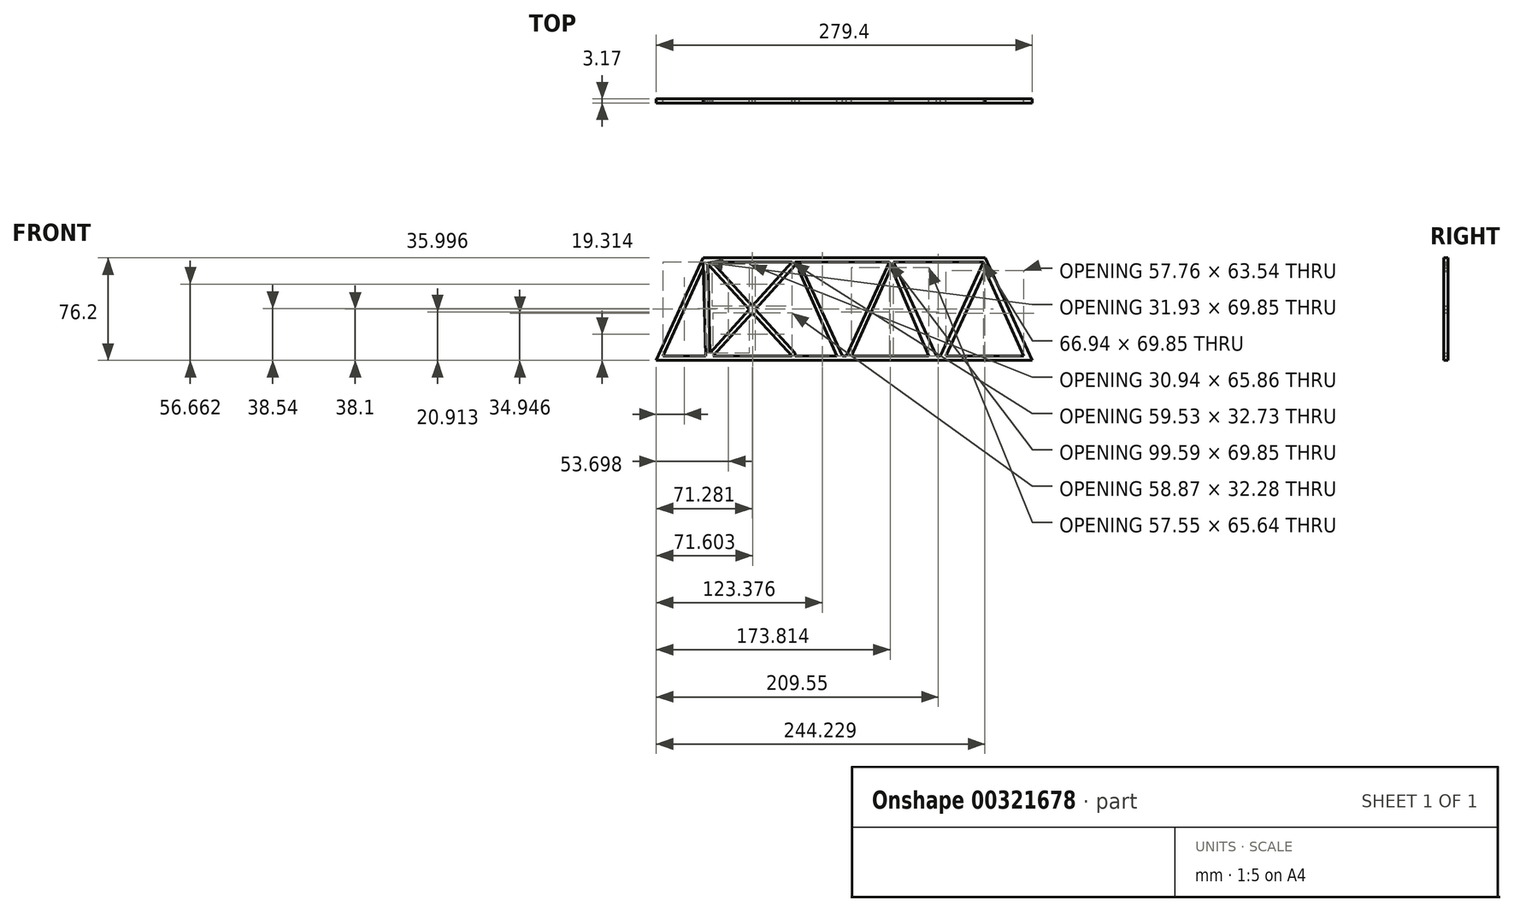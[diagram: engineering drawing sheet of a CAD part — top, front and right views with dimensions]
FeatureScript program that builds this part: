
annotation { "Feature Type Name" : "Feature", "Feature Type Description" : "" }
export const myFeature = defineFeature(function(context is Context, id is Id, definition is map)
    precondition{}
    {
        {
            var Q0;
            Q0=qCreatedBy(makeId("Front.planeOp"),FACE);
            var sketch = newSketch(context, id + "F0", { "sketchPlane" : qUnion([Q0])});
            skLineSegment(sketch, "E0", {"start": v(-139.7, 0) * mm, "end": v(139.7, 0) * mm});
            skLineSegment(sketch, "E1", {"start": v(-139.7, 0) * mm, "end": v(-104.78, 76.2) * mm});
            skLineSegment(sketch, "E2", {"start": v(-101.6, 76.2) * mm, "end": v(104.78, 76.2) * mm});
            skLineSegment(sketch, "E3", {"start": v(104.77, 76.2) * mm, "end": v(139.7, 0) * mm});
            skLineSegment(sketch, "E4", {"start": v(-1.46, 3.18) * mm, "end": v(-33.47, 73.03) * mm});
            skLineSegment(sketch, "E5", {"start": v(1.46, 3.18) * mm, "end": v(33.47, 73.03) * mm});
            skLineSegment(sketch, "E6", {"start": v(36.38, 73.03) * mm, "end": v(68.4, 3.17) * mm});
            skLineSegment(sketch, "E7", {"start": v(71.3, 3.17) * mm, "end": v(103.32, 73.03) * mm});
            skLineSegment(sketch, "E8", {"start": v(34.92, 73.03) * mm, "end": v(34.92, 3.17) * mm});
            skLineSegment(sketch, "E9", {"start": v(69.85, 3.17) * mm, "end": v(69.85, 76.2) * mm});
            skLineSegment(sketch, "E10", {"start": v(104.78, 76.2) * mm, "end": v(104.78, 0) * mm});
            skLineSegment(sketch, "E11", {"start": v(-104.76, 68.62) * mm, "end": v(-134.75, 3.18) * mm});
            skLineSegment(sketch, "E12", {"start": v(-134.75, 3.18) * mm, "end": v(-102.82, 3.18) * mm});
            skLineSegment(sketch, "E13.MirrorCS", {"start": v(-71.44, 3.18) * mm, "end": v(-99.65, 3.17) * mm});
            skLineSegment(sketch, "E14", {"start": v(-101.51, 73.03) * mm, "end": v(104.78, 73.03) * mm});
            skPoint(sketch, "E15.orphan", {"position": v(-34.93, 76.2) * mm});
            skPoint(sketch, "E16.orphan", {"position": v(34.92, 76.2) * mm});
            skLineSegment(sketch, "E17", {"start": v(-104.78, 76.2) * mm, "end": v(-104.76, 73.03) * mm});
            skLineSegment(sketch, "E18", {"start": v(-104.76, 73.03) * mm, "end": v(-104.76, 68.62) * mm});
            skLineSegment(sketch, "E19", {"start": v(-104.76, 73.03) * mm, "end": v(-104.7, 73.02) * mm});
            skLineSegment(sketch, "E20", {"start": v(-104.78, 76.2) * mm, "end": v(-102.82, 3.17) * mm});
            skLineSegment(sketch, "E21", {"start": v(-101.6, 76.2) * mm, "end": v(-99.65, 3.17) * mm});
            skLineSegment(sketch, "E22", {"start": v(-104.78, 76.2) * mm, "end": v(-101.6, 76.2) * mm});
            skLineSegment(sketch, "E23", {"start": v(-102.82, 3.17) * mm, "end": v(-99.65, 3.17) * mm});
            skLineSegment(sketch, "E24", {"start": v(-71.44, 3.18) * mm, "end": v(138.24, 3.18) * mm});
            skPoint(sketch, "E25.start.orphan", {"position": v(-69.85, 0) * mm});
            skPoint(sketch, "E26.orphan", {"position": v(0, 0) * mm});
            skPoint(sketch, "E27.orphan", {"position": v(69.85, 0) * mm});
            skLineSegment(sketch, "E28.bottom", {"start": v(-36.51, 3.18) * mm, "end": v(-33.34, 3.18) * mm});
            skLineSegment(sketch, "E28.top", {"start": v(-36.51, 73.03) * mm, "end": v(-33.34, 73.03) * mm});
            skLineSegment(sketch, "E28.left", {"start": v(-36.51, 3.17) * mm, "end": v(-36.51, 73.02) * mm});
            skLineSegment(sketch, "E28.right", {"start": v(-33.34, 3.17) * mm, "end": v(-33.34, 73.02) * mm});
            skLineSegment(sketch, "E29.0", {"start": v(-98.19, 73.03) * mm, "end": v(-68.3, 40.3) * mm});
            skLineSegment(sketch, "E30.0", {"start": v(-101.47, 71.47) * mm, "end": v(-70.53, 37.83) * mm});
            skLineSegment(sketch, "E31.trimOffspring", {"start": v(-66.12, 37.92) * mm, "end": v(-36.51, 5.5) * mm});
            skLineSegment(sketch, "E32.trimOffspring", {"start": v(-68.35, 35.45) * mm, "end": v(-38.66, 3.17) * mm});
            skLineSegment(sketch, "E33.0", {"start": v(-38.65, 73.03) * mm, "end": v(-68.3, 40.3) * mm});
            skLineSegment(sketch, "E34.0", {"start": v(-36.51, 70.66) * mm, "end": v(-68.27, 35.54) * mm});
            skLineSegment(sketch, "E35.trimOffspring", {"start": v(-70.53, 37.83) * mm, "end": v(-99.71, 5.61) * mm});
            skLineSegment(sketch, "E36.trimOffspring", {"start": v(-68.23, 35.58) * mm, "end": v(-97.53, 3.17) * mm});
            skLineSegment(sketch, "E37", {"start": v(-70.53, 37.83) * mm, "end": v(-68.3, 40.3) * mm});
            skLineSegment(sketch, "E38", {"start": v(-33.34, 66.1) * mm, "end": v(-5.54, 3.18) * mm});
            skLineSegment(sketch, "E39", {"start": v(5.34, 3.17) * mm, "end": v(34.92, 68.82) * mm});
            skLineSegment(sketch, "E40", {"start": v(62.89, 3.18) * mm, "end": v(34.92, 68.82) * mm});
            skLineSegment(sketch, "E41", {"start": v(75.65, 3.17) * mm, "end": v(104.78, 66.72) * mm});
            skLineSegment(sketch, "E42", {"start": v(104.78, 66.72) * mm, "end": v(133.4, 3.18) * mm});
            skSolve(sketch);
        }
        {
            var Q0;
            Q0 = qSketchRegion(id + "F0", true);
            var Q1;
            {var subQ1=sQuery(id+"F0.wireOp",EDGE,"E7");Q1=makeQuery(id+"F0.imprint","IMPRINT",FACE,{"disambiguationData":[TD([[makeQuery(id+"F0.imprint","IMPRINT",EDGE,{"derivedFrom":subQ1}),-1.0]])]});}
            var Q2;
            {var subQ1=sQuery(id+"F0.wireOp",EDGE,"E6");Q2=makeQuery(id+"F0.imprint","IMPRINT",FACE,{"disambiguationData":[TD([[makeQuery(id+"F0.imprint","IMPRINT",EDGE,{"derivedFrom":subQ1}),-1.0]])]});}
            var Q3;
            {var subQ1=sQuery(id+"F0.wireOp",EDGE,"E5");Q3=makeQuery(id+"F0.imprint","IMPRINT",FACE,{"disambiguationData":[TD([[makeQuery(id+"F0.imprint","IMPRINT",EDGE,{"derivedFrom":subQ1}),-1.0]])]});}
            var Q4;
            {var subQ5=sQuery(id+"F0.wireOp",EDGE,"E38");Q4=makeQuery(id+"F0.imprint","IMPRINT",FACE,{"disambiguationData":[TD([[makeQuery(id+"F0.imprint","IMPRINT",EDGE,{"derivedFrom":subQ5}),1.0]])]});}
            var Q5;
            {var subQ1=sQuery(id+"F0.wireOp",EDGE,"E28.bottom");Q5=makeQuery(id+"F0.imprint","IMPRINT",FACE,{"disambiguationData":[TD([[makeQuery(id+"F0.imprint","IMPRINT",EDGE,{"derivedFrom":subQ1}),1.0]])]});}
            var Q6;
            {var subQ8=sQuery(id+"F0.wireOp",EDGE,"E33.0");Q6=makeQuery(id+"F0.imprint","IMPRINT",FACE,{"disambiguationData":[TD([[makeQuery(id+"F0.imprint","IMPRINT",EDGE,{"derivedFrom":subQ8}),1.0]])]});}
            var Q7;
            {var subQ4=sQuery(id+"F0.wireOp",EDGE,"E31.trimOffspring");Q7=makeQuery(id+"F0.imprint","IMPRINT",FACE,{"disambiguationData":[TD([[makeQuery(id+"F0.imprint","IMPRINT",EDGE,{"derivedFrom":subQ4}),-1.0]])]});}
            var Q8;
            {var subQ0=sQuery(id+"F0.wireOp",EDGE,"E29.0");Q8=makeQuery(id+"F0.imprint","IMPRINT",FACE,{"disambiguationData":[TD([[makeQuery(id+"F0.imprint","IMPRINT",EDGE,{"derivedFrom":subQ0}),-1.0]])]});}
            extrude(context, id + "F1", {"entities" : qUnion([Q0, Q1, Q2, Q3, Q4, Q5, Q6, Q7, Q8]), "depth" : 3.17 * mm});
        }
    });
